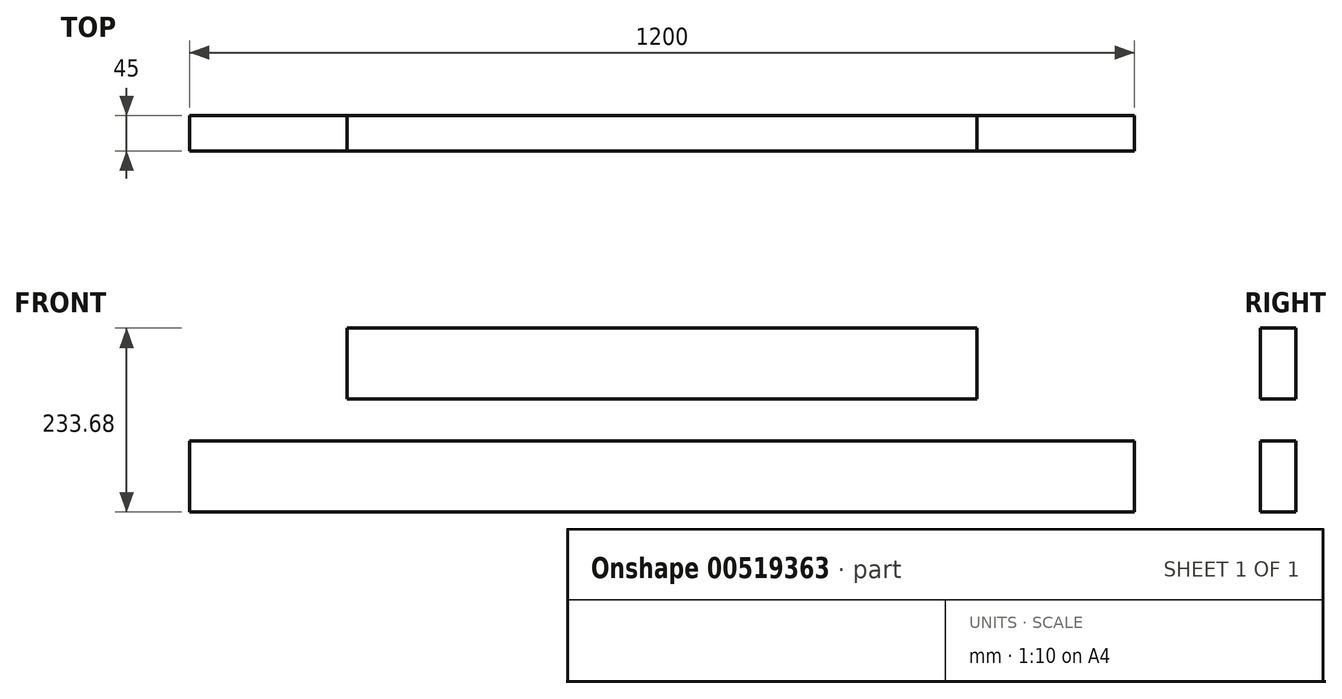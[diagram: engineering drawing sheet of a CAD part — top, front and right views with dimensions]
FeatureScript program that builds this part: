
annotation { "Feature Type Name" : "Feature", "Feature Type Description" : "" }
export const myFeature = defineFeature(function(context is Context, id is Id, definition is map)
    precondition{}
    {
        {
            var Q0;
            Q0=qCreatedBy(makeId("Front.planeOp"),FACE);
            var sketch = newSketch(context, id + "F0", { "sketchPlane" : qUnion([Q0])});
            skLineSegment(sketch, "E0.bottom", {"start": v(-600, 45) * mm, "end": v(600, 45) * mm});
            skLineSegment(sketch, "E0.top", {"start": v(-600, -45) * mm, "end": v(600, -45) * mm});
            skLineSegment(sketch, "E0.left", {"start": v(-600, 45) * mm, "end": v(-600, -45) * mm});
            skLineSegment(sketch, "E0.right", {"start": v(600, 45) * mm, "end": v(600, -45) * mm});
            skPoint(sketch, "E0.middle", {"position": v(0, 0) * mm});
            skSolve(sketch);
        }
        {
            var Q0;
            Q0=makeQuery(id+"F0.imprint","IMPRINT",FACE,{"disambiguationData":[TD([[makeQuery(id+"F0.imprint","IMPRINT",EDGE,{"derivedFrom":sQuery(id+"F0.wireOp",EDGE,"E0.bottom")}),-1.0]])]});
            extrude(context, id + "F1", {"entities" : qUnion([Q0]), "depth" : 45 * mm, "offsetDistance" : 25 * mm});
        }
        {
            var Q0;
            Q0=qCreatedBy(makeId("Front.planeOp"),FACE);
            var sketch = newSketch(context, id + "F2", { "sketchPlane" : qUnion([Q0])});
            skLineSegment(sketch, "E1.bottom", {"start": v(-400, 188.68) * mm, "end": v(400, 188.68) * mm});
            skLineSegment(sketch, "E1.top", {"start": v(-400, 98.68) * mm, "end": v(400, 98.68) * mm});
            skLineSegment(sketch, "E1.left", {"start": v(-400, 188.68) * mm, "end": v(-400, 98.68) * mm});
            skLineSegment(sketch, "E1.right", {"start": v(400, 188.68) * mm, "end": v(400, 98.68) * mm});
            skPoint(sketch, "E1.middle", {"position": v(0, 143.68) * mm});
            skSolve(sketch);
        }
        {
            var Q0;
            Q0=makeQuery(id+"F2.imprint","IMPRINT",FACE,{"disambiguationData":[TD([[makeQuery(id+"F2.imprint","IMPRINT",EDGE,{"derivedFrom":sQuery(id+"F2.wireOp",EDGE,"E1.bottom")}),-1.0]])]});
            extrude(context, id + "F3", {"entities" : qUnion([Q0]), "depth" : 45 * mm, "offsetDistance" : 25 * mm});
        }
    });
